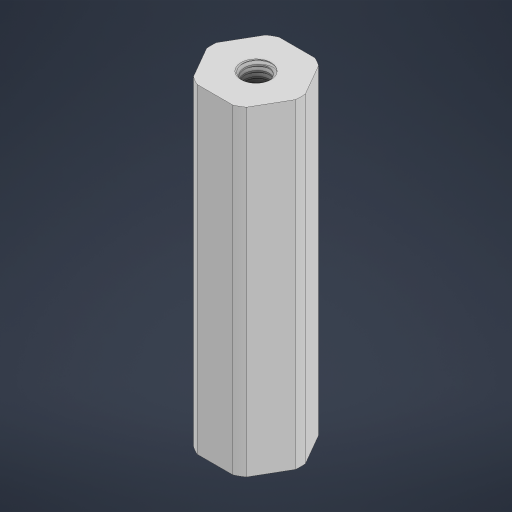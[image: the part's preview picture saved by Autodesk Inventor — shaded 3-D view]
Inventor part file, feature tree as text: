
AUTODESK INVENTOR PART (.ipt)
format: ipt  version: 2023 (Build 270158000, 158)  size: 1,017,344 bytes
history: native  units: in
note: dims shown in document units (in); Inventor stores cm internally (conversion verified against a paired STEP export)
features: mirror x1
ambient origin geometry x8: Origin, YZ Plane, XZ Plane, XY Plane, X Axis, Y Axis, Z Axis, Center Point
bodies: Solid1 (feature_tree)
feature tree (1):
  mirror  "Mirror2"
